# Revit family: Б408_RV17_LOD400 (04.11.23)
name_source: partatom
category: Электрооборудование
revit_build: Autodesk Revit 2017 (Build: 20170118_1100(x64)
units: mm (PartAtom-declared; Revit-internal decimal feet)

## family parameters
Всегда вертикально = Нет
Конфигурация панели = Два столбца, слева направо
На основе рабочей плоскости = Да
Общий = Нет
При загрузке вырезать с полостями = Нет
Размер круглого соединителя = Использовать диаметр
Тип детали = Щит
Точка расчета площади = Нет

## types (1)
- Б408
    ADSK_URL страницы изделия = https://stilsoft.ru
    ADSK_Единица измерения = шт.
    ADSK_Завод-изготовитель = ООО «Основа Безопасности»
    ADSK_Количество = 1
    ADSK_Марка = СТВФ.426484.040ПС
    ADSK_Масса = 0.7
    ADSK_Наименование = Контроллер Б408
    ADSK_Размер_Высота = 42 мм
    ADSK_Размер_Глубина = 92 мм
    ADSK_Размер_Длина = 197 мм
    d_короба = 20 мм
    Интерфейс для подключения внешних устройств = RS-485
    Интерфейс считывающих устройств = Wiegand 26, Wiegand 40/42
    Количество подключаемых считывающих устройств, не более, шт. = 4
    Количество подключаемых устройств, управляемых преграждающих (или исполнительных), шт. = 2
    Количество реле, шт = 4
    Максимальное количество ключей (пропусков) = 40000
    Максимальное количество подключаемых извещателей = 8
    Максимальное удаление считывающих устройств от контролера, не более, м = 100 мм
    Максимальный потребляемый контроллером ток от сети постоянного тока (без дополнительных внешних потребителей), А = 0 А
    Максимальный ток, проходящий через реле для 220В, не более, А = 2 А
    Максимальный ток, проходящий через реле для 28В, не более, А = 4 А
    Напряжение = 12
    Отметка по умолчанию = 1219 мм
    Стандарт интерфейса связи = 10 Base-T Ethernet (гнездо RJ-45)
